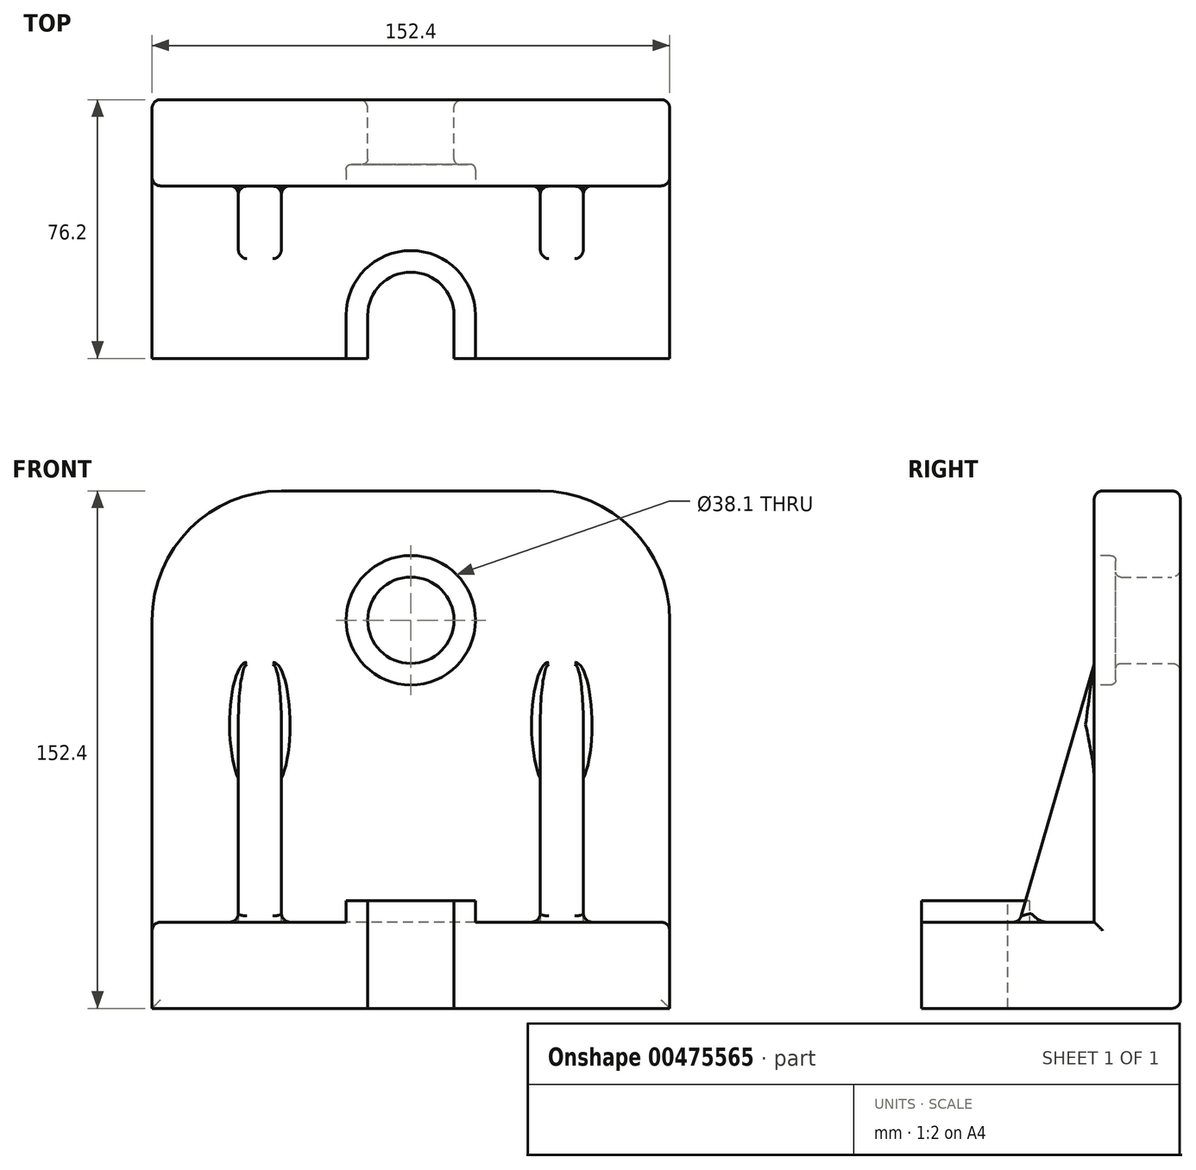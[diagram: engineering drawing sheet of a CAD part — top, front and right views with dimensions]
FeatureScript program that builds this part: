
annotation { "Feature Type Name" : "Feature", "Feature Type Description" : "" }
export const myFeature = defineFeature(function(context is Context, id is Id, definition is map)
    precondition{}
    {
        {
            var Q0;
            Q0=qCreatedBy(makeId("Right.planeOp"),FACE);
            var sketch = newSketch(context, id + "F0", { "sketchPlane" : qUnion([Q0])});
            skLineSegment(sketch, "E0", {"start": v(0, 0) * mm, "end": v(-76.2, 0) * mm});
            skLineSegment(sketch, "E1", {"start": v(-76.2, 0) * mm, "end": v(-76.2, 25.4) * mm});
            skLineSegment(sketch, "E2", {"start": v(-25.4, 152.4) * mm, "end": v(0, 152.4) * mm});
            skLineSegment(sketch, "E3", {"start": v(0, 152.4) * mm, "end": v(0, 0) * mm});
            skLineSegment(sketch, "E4", {"start": v(-25.4, 152.4) * mm, "end": v(-25.4, 25.4) * mm});
            skLineSegment(sketch, "E5", {"start": v(-25.4, 25.4) * mm, "end": v(-76.2, 25.4) * mm});
            skSolve(sketch);
        }
        {
            var Q0;
            Q0 = qSketchRegion(id + "F0", true);
            extrude(context, id + "F1", {"entities" : qUnion([Q0]), "endBound" : BoundingType.SYMMETRIC, "depth" : 152.4 * mm});
        }
        {
            var Q0;
            Q0=makeQuery(id+"F1.opExtrude","SWEPT_FACE",FACE,{"disambiguationData":[OSD([sQuery(id+"F0.wireOp",EDGE,"E3")])]});
            var sketch = newSketch(context, id + "F2", { "sketchPlane" : qUnion([Q0])});
            skCircle(sketch, "E6", {"center": v(0, 114.3) * mm, "radius": 12.7 * mm});
            skSolve(sketch);
        }
        {
            var Q0;
            Q0 = qSketchRegion(id + "F2", true);
            extrude(context, id + "F3", {"entities" : qUnion([Q0]), "operationType" : NewBodyOperationType.REMOVE, "oppositeDirection" : true, "depth" : 25.4 * mm});
        }
        {
            var Q0;
            Q0=makeQuery(id+"F1.opExtrude","CAP_EDGE",EDGE,{"disambiguationData":[OSD([sQuery(id+"F0.wireOp",EDGE,"E2")])],"isStart":true});
            var Q1;
            Q1=makeQuery(id+"F1.opExtrude","CAP_EDGE",EDGE,{"disambiguationData":[OSD([sQuery(id+"F0.wireOp",EDGE,"E2")])],"isStart":false});
            fillet(context, id + "F4", {"entities" : qUnion([Q0, Q1]), "radius" : 38.1 * mm, "tangentPropagation" : true, "allowEdgeOverflow" : false});
        }
        {
            var Q0;
            Q0=makeQuery(id+"F1.opExtrude","SWEPT_FACE",FACE,{"disambiguationData":[OSD([sQuery(id+"F0.wireOp",EDGE,"E5")])]});
            var sketch = newSketch(context, id + "F5", { "sketchPlane" : qUnion([Q0])});
            skLineSegment(sketch, "E7.bottom", {"start": v(12.7, -76.2) * mm, "end": v(-12.7, -76.2) * mm});
            skLineSegment(sketch, "E7.left", {"start": v(12.7, -76.2) * mm, "end": v(12.7, -63.5) * mm});
            skLineSegment(sketch, "E7.right", {"start": v(-12.7, -76.2) * mm, "end": v(-12.7, -63.5) * mm});
            skArc(sketch, "E8", {"start": v(12.7, -63.5) * mm, "mid": v(0, -50.8) * mm, "end": v(-12.7, -63.5) * mm});
            skSolve(sketch);
        }
        {
            var Q0;
            Q0 = qSketchRegion(id + "F5", true);
            extrude(context, id + "F6", {"entities" : qUnion([Q0]), "operationType" : NewBodyOperationType.REMOVE, "endBound" : BoundingType.THROUGH_ALL, "oppositeDirection" : true, "depth" : 25.4 * mm});
        }
        {
            var Q0;
            Q0=makeQuery(id+"F1.opExtrude","SWEPT_FACE",FACE,{"disambiguationData":[OSD([sQuery(id+"F0.wireOp",EDGE,"E4")])]});
            var sketch = newSketch(context, id + "F7", { "sketchPlane" : qUnion([Q0])});
            skCircle(sketch, "E9", {"center": v(0, 114.3) * mm, "radius": 19.05 * mm});
            skSolve(sketch);
        }
        {
            var Q0;
            Q0 = qSketchRegion(id + "F7", true);
            extrude(context, id + "F8", {"entities" : qUnion([Q0]), "operationType" : NewBodyOperationType.REMOVE, "oppositeDirection" : true, "depth" : 6.35 * mm});
        }
        {
            var Q0;
            Q0=qCreatedBy(makeId("Right.planeOp"),FACE);
            cPlane(context, id + "F9", {"entities" : qUnion([Q0]), "cplaneType" : CPlaneType.OFFSET, "offset" : 44.45 * mm, "width" : 152.4 * mm, "height" : 152.4 * mm});
        }
        {
            var Q0;
            Q0=qCreatedBy(id+"F9.planeOp",FACE);
            var sketch = newSketch(context, id + "F10", { "sketchPlane" : qUnion([Q0])});
            skLineSegment(sketch, "E10", {"start": v(-47.38, 25.4) * mm, "end": v(-25.4, 101.6) * mm});
            skLineSegment(sketch, "E11", {"start": v(-25.4, 101.6) * mm, "end": v(-25.4, 25.4) * mm});
            skLineSegment(sketch, "E12", {"start": v(-25.4, 25.4) * mm, "end": v(-47.38, 25.4) * mm});
            skSolve(sketch);
        }
        {
            var Q0;
            Q0=makeQuery(id+"F10.imprint","IMPRINT",FACE,{"disambiguationData":[TD([[makeQuery(id+"F10.imprint","IMPRINT",EDGE,{"derivedFrom":sQuery(id+"F10.wireOp",EDGE,"E10")}),-1.0]])]});
            extrude(context, id + "F11", {"entities" : qUnion([Q0]), "operationType" : NewBodyOperationType.ADD, "endBound" : BoundingType.SYMMETRIC, "depth" : 12.7 * mm});
        }
        {
            var Q0;
            Q0=makeQuery(id+"F1.opExtrude","SWEPT_BODY",BODY,{"disambiguationData":[OSD([sQuery(id+"F0.wireOp",EDGE,"E0"),sQuery(id+"F0.wireOp",EDGE,"E1"),sQuery(id+"F0.wireOp",EDGE,"E2"),sQuery(id+"F0.wireOp",EDGE,"E3"),sQuery(id+"F0.wireOp",EDGE,"E4"),sQuery(id+"F0.wireOp",EDGE,"E5")])]});
            var Q1;
            Q1=qCreatedBy(makeId("Right.planeOp"),FACE);
            mirror(context, id + "F12", {"operationType" : NewBodyOperationType.ADD, "entities" : qUnion([Q0]), "mirrorPlane" : qUnion([Q1])});
        }
        {
            var Q0;
            Q0=makeQuery(id+"F8.boolean.opBoolean","INTERSECT",EDGE,{"derivedFrom":[makeQuery(id+"F3.boolean.opBoolean","COPY",FACE,{"derivedFrom":makeQuery(id+"F3.opExtrude","SWEPT_FACE",FACE,{"disambiguationData":[OSD([sQuery(id+"F2.wireOp",EDGE,"E6")])]})}),makeQuery(id+"F8.opExtrude","CAP_FACE",FACE,{"disambiguationData":[OSD([sQuery(id+"F7.wireOp",EDGE,"E9")])],"isStart":false})]});
            var Q1;
            Q1=makeQuery(id+"F8.boolean.opBoolean","COPY",EDGE,{"derivedFrom":makeQuery(id+"F8.opExtrude","CAP_EDGE",EDGE,{"disambiguationData":[OSD([sQuery(id+"F7.wireOp",EDGE,"E9")])],"isStart":false})});
            fillet(context, id + "F13", {"entities" : qUnion([Q0, Q1]), "radius" : 1.52 * mm, "tangentPropagation" : true, "allowEdgeOverflow" : false});
        }
        {
            var Q0;
            Q0=makeQuery(id+"F1.opExtrude","SWEPT_FACE",FACE,{"disambiguationData":[OSD([sQuery(id+"F0.wireOp",EDGE,"E5")])]});
            var sketch = newSketch(context, id + "F14", { "sketchPlane" : qUnion([Q0])});
            skLineSegment(sketch, "E13.0", {"start": v(-19.05, -76.2) * mm, "end": v(-19.05, -63.5) * mm});
            skArc(sketch, "E13.1", {"start": v(19.05, -63.5) * mm, "mid": v(0, -44.45) * mm, "end": v(-19.05, -63.5) * mm});
            skLineSegment(sketch, "E13.2", {"start": v(19.05, -76.2) * mm, "end": v(19.05, -63.5) * mm});
            skSolve(sketch);
        }
        {
            var Q0;
            Q0 = qSketchRegion(id + "F14", true);
            var Q1;
            {var subQ3=sQuery(id+"F14.wireOp",EDGE,"E13.0");Q1=makeQuery(id+"F14.imprint","IMPRINT",FACE,{"disambiguationData":[TD([[makeQuery(id+"F14.imprint","IMPRINT",EDGE,{"derivedFrom":subQ3}),-1.0]])]});}
            extrude(context, id + "F15", {"entities" : qUnion([Q0, Q1]), "operationType" : NewBodyOperationType.ADD, "depth" : 6.35 * mm});
        }
        {
            var Q0;
            Q0=makeQuery(id+"F15.opExtrude","CAP_EDGE",EDGE,{"disambiguationData":[OSD([sQuery(id+"F14.wireOp",EDGE,"E13.0")])],"isStart":true});
            var Q1;
            Q1=makeQuery(id+"F12.opPattern","COPY",FACE,{"derivedFrom":makeQuery(id+"F11.opExtrude","SWEPT_FACE",FACE,{"disambiguationData":[OSD([sQuery(id+"F10.wireOp",EDGE,"E10")])]}),"instanceName":"1"});
            var Q2;
            Q2=makeQuery(id+"F11.opExtrude","SWEPT_FACE",FACE,{"disambiguationData":[OSD([sQuery(id+"F10.wireOp",EDGE,"E10")])]});
            var Q3;
            Q3=makeQuery(id+"F15.opExtrude","CAP_EDGE",EDGE,{"disambiguationData":[OSD([sQuery(id+"F14.wireOp",EDGE,"E13.2")])],"isStart":true});
            var Q4;
            Q4=makeQuery(id+"F15.opExtrude","CAP_EDGE",EDGE,{"disambiguationData":[OSD([sQuery(id+"F14.wireOp",EDGE,"E13.1")])],"isStart":true});
            var Q5;
            Q5=makeQuery(id+"F1.opExtrude","CAP_EDGE",EDGE,{"disambiguationData":[OSD([sQuery(id+"F0.wireOp",EDGE,"E5")])],"isStart":true});
            var Q6;
            Q6=makeQuery(id+"F1.opExtrude","CAP_EDGE",EDGE,{"disambiguationData":[OSD([sQuery(id+"F0.wireOp",EDGE,"E4")])],"isStart":true});
            var Q7;
            Q7=makeQuery(id+"F1.opExtrude","CAP_EDGE",EDGE,{"disambiguationData":[OSD([sQuery(id+"F0.wireOp",EDGE,"E5")])],"isStart":false});
            var Q8;
            Q8=makeQuery(id+"F1.opExtrude","CAP_EDGE",EDGE,{"disambiguationData":[OSD([sQuery(id+"F0.wireOp",EDGE,"E4")])],"isStart":false});
            var Q9;
            Q9=makeQuery(id+"F4.opFillet","BLEND_EDGE",EDGE,{"blendedFrom":[makeQuery(id+"F1.opExtrude","CAP_EDGE",EDGE,{"disambiguationData":[OSD([sQuery(id+"F0.wireOp",EDGE,"E2")])],"isStart":false}),makeQuery(id+"F1.opExtrude","SWEPT_FACE",FACE,{"disambiguationData":[OSD([sQuery(id+"F0.wireOp",EDGE,"E4")])]})],"blendedInto":[makeQuery(id+"F1.opExtrude","SWEPT_FACE",FACE,{"disambiguationData":[OSD([sQuery(id+"F0.wireOp",EDGE,"E4")])]})]});
            var Q10;
            Q10=makeQuery(id+"F1.opExtrude","SWEPT_EDGE",EDGE,{"disambiguationData":[OSD([sQuery(id+"F0.wireOp",EDGE,"E2"),sQuery(id+"F0.wireOp",EDGE,"E4")])]});
            var Q11;
            Q11=makeQuery(id+"F4.opFillet","BLEND_EDGE",EDGE,{"blendedFrom":[makeQuery(id+"F1.opExtrude","CAP_EDGE",EDGE,{"disambiguationData":[OSD([sQuery(id+"F0.wireOp",EDGE,"E2")])],"isStart":true}),makeQuery(id+"F1.opExtrude","SWEPT_FACE",FACE,{"disambiguationData":[OSD([sQuery(id+"F0.wireOp",EDGE,"E4")])]})],"blendedInto":[makeQuery(id+"F1.opExtrude","SWEPT_FACE",FACE,{"disambiguationData":[OSD([sQuery(id+"F0.wireOp",EDGE,"E4")])]})]});
            var Q12;
            Q12=makeQuery(id+"F1.opExtrude","SWEPT_FACE",FACE,{"disambiguationData":[OSD([sQuery(id+"F0.wireOp",EDGE,"E3")])]});
            fillet(context, id + "F16", {"entities" : qUnion([Q0, Q1, Q2, Q3, Q4, Q5, Q6, Q7, Q8, Q9, Q10, Q11, Q12]), "radius" : 2.54 * mm, "allowEdgeOverflow" : false});
        }
    });
